# Revit family: 35814-presto
name_source: partatom
category: Plumbing Fixtures
units: mm (PartAtom-declared; Revit-internal decimal feet)

## family parameters
Always vertical = Yes
Cut with Voids When Loaded = No
Maintain Annotation Orientation = No
OmniClass Number = 23.45.00.00
OmniClass Title = Sanitary, Laundry, and Cleaning Equipment
Part Type = Normal
Room Calculation Point = No
Round Connector Dimension = Use Diameter
Shared = No
Work Plane-Based = Yes

## types (1)
- 35814- Les Robinets PRESTO
    - Hydraulic supply = 20.00 mm
    Default Elevation = 1219 mm
    Description = 2 Filter gaskets
3 Union nuts 3/4" (20x27)
2 angled connectors M 3/4" - F 1/2
    Model = 35814
    Recommended pressure = 3.0 Pa
    URL = https://www.prestodatashare.com
    brand = Les Robinets PRESTO
    flow time = 30.0 s
    material = Chrome-plated knob
    min flow = 8.0 L/min
    min pressure = 1.0 Pa
    pressure = 5.0 Pa
    range = Sanitary accessories
    ref = Ref: 35814 - Wall mounted PRESTO ALPA mixer tap

## geometry (parser evidence)
native form markers: Sweep x2
no freeform markers — native parametric forms only
